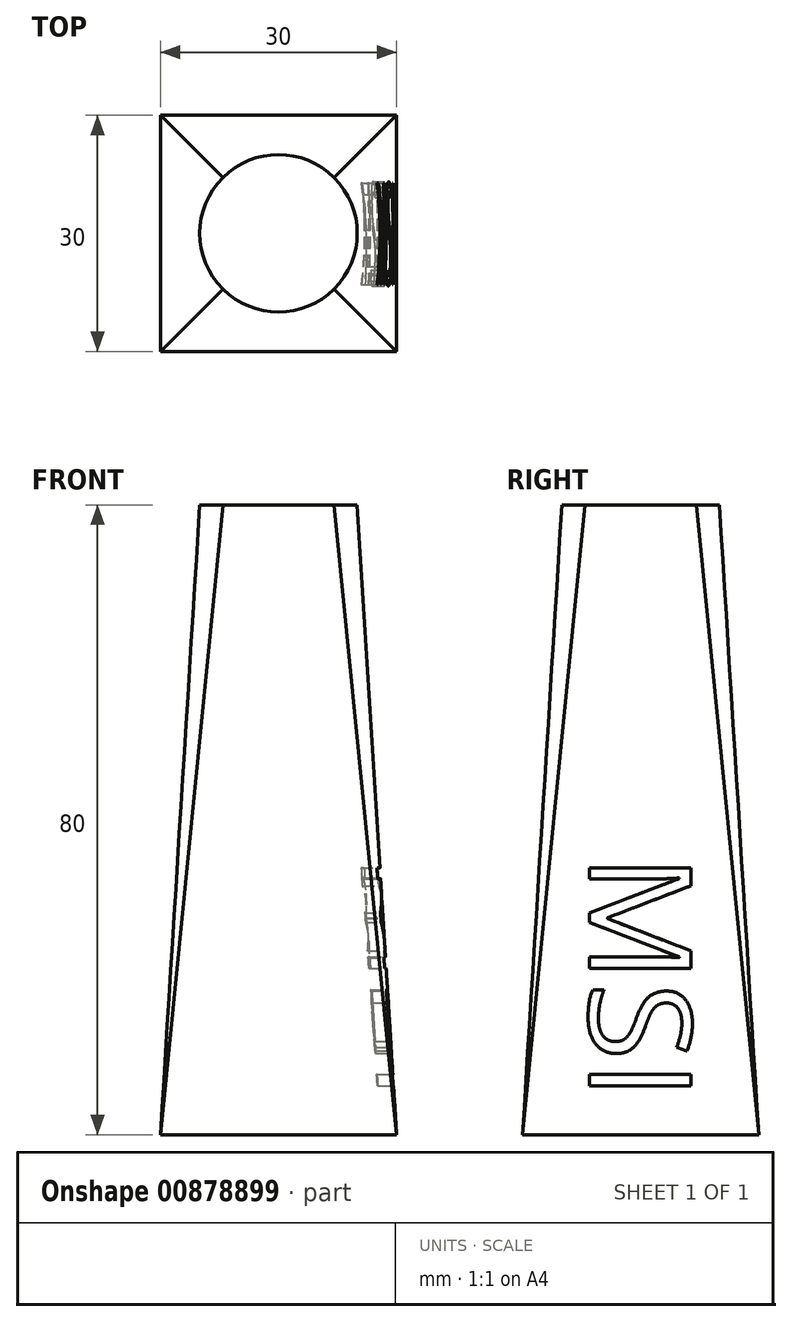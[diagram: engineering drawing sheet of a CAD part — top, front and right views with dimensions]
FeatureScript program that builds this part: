
annotation { "Feature Type Name" : "Feature", "Feature Type Description" : "" }
export const myFeature = defineFeature(function(context is Context, id is Id, definition is map)
    precondition{}
    {
        {
            var Q0;
            Q0=qCreatedBy(makeId("Top.planeOp"),FACE);
            var sketch = newSketch(context, id + "F0", { "sketchPlane" : qUnion([Q0])});
            skLineSegment(sketch, "E0.bottom", {"start": v(15, -15) * mm, "end": v(-15, -15) * mm});
            skLineSegment(sketch, "E0.top", {"start": v(15, 15) * mm, "end": v(-15, 15) * mm});
            skLineSegment(sketch, "E0.left", {"start": v(15, -15) * mm, "end": v(15, 15) * mm});
            skLineSegment(sketch, "E0.right", {"start": v(-15, -15) * mm, "end": v(-15, 15) * mm});
            skPoint(sketch, "E0.middle", {"position": v(0, 0) * mm});
            skSolve(sketch);
        }
        {
            var Q0;
            Q0=qCreatedBy(makeId("Top.planeOp"),FACE);
            cPlane(context, id + "F1", {"entities" : qUnion([Q0]), "cplaneType" : CPlaneType.OFFSET, "offset" : 80 * mm, "width" : 150 * mm, "height" : 150 * mm});
        }
        {
            var Q0;
            Q0=qCreatedBy(id+"F1.planeOp",FACE);
            var sketch = newSketch(context, id + "F2", { "sketchPlane" : qUnion([Q0])});
            skCircle(sketch, "E1", {"center": v(0, 0) * mm, "radius": 10 * mm});
            skSolve(sketch);
        }
        {
            var Q0;
            Q0=makeQuery(id+"F0.imprint","IMPRINT",FACE,{"disambiguationData":[TD([[makeQuery(id+"F0.imprint","IMPRINT",EDGE,{"derivedFrom":sQuery(id+"F0.wireOp",EDGE,"E0.bottom")}),-1.0]])]});
            var Q1;
            Q1=makeQuery(id+"F2.imprint","IMPRINT",FACE,{"disambiguationData":[TD([[makeQuery(id+"F2.imprint","IMPRINT",EDGE,{"derivedFrom":sQuery(id+"F2.wireOp",EDGE,"E1")}),1.0]])]});
            loft(context, id + "F3", {"sheetProfilesArray" : [{ "sheetProfileEntities" : qUnion([Q0]) }, { "sheetProfileEntities" : qUnion([Q1]) }]});
        }
        {
            var Q0;
            Q0=qCreatedBy(makeId("Right.planeOp"),FACE);
            cPlane(context, id + "F4", {"entities" : qUnion([Q0]), "cplaneType" : CPlaneType.OFFSET, "offset" : 50 * mm, "width" : 150 * mm, "height" : 150 * mm});
        }
        {
            var Q0;
            Q0=qCreatedBy(id+"F4.planeOp",FACE);
            var sketch = newSketch(context, id + "F5", { "sketchPlane" : qUnion([Q0])});
            skText(sketch, "E2", { "text": "MSI", "fontName": "OpenSans-Regular.ttf"});
            const initialGuessF5  = {"E2": [-0.0065, 0.03565, 0, -1, 0.013]};
            skSetInitialGuess(sketch, initialGuessF5);
            skSolve(sketch);
        }
        {
            var Q0;
            Q0 = qSketchRegion(id + "F5", true);
            var Q1;
            Q1 = qConstructionFilter(qBodyType(qCreatedBy(id + "F5" ,EDGE), BodyType.WIRE), ConstructionObject.NO);
            var Q2;
            Q2=makeQuery(id+"F3.opLoft","SWEPT_FACE",FACE,{"disambiguationData":[OSD([sQuery(id+"F0.wireOp",EDGE,"E0.bottom"),sQuery(id+"F0.wireOp",EDGE,"E0.top"),sQuery(id+"F0.wireOp",EDGE,"E0.left"),sQuery(id+"F2.wireOp",EDGE,"E1")])]});
            var Q3;
            Q3=makeQuery(id+"F3.opLoft","SWEPT_BODY",BODY,{"disambiguationData":[OSD([makeQuery(id+"F0.imprint","IMPRINT",FACE,{"disambiguationData":[TD([[makeQuery(id+"F0.imprint","IMPRINT",EDGE,{"derivedFrom":sQuery(id+"F0.wireOp",EDGE,"E0.bottom")}),-1.0]])]}),makeQuery(id+"F2.imprint","IMPRINT",FACE,{"disambiguationData":[TD([[makeQuery(id+"F2.imprint","IMPRINT",EDGE,{"derivedFrom":sQuery(id+"F2.wireOp",EDGE,"E1")}),1.0]])]})])]});
            extrude(context, id + "F6", {"entities" : qUnion([Q0]), "operationType" : NewBodyOperationType.REMOVE, "surfaceEntities" : qUnion([Q1]), "endBound" : BoundingType.UP_TO_BODY, "oppositeDirection" : true, "depth" : 25 * mm, "endBoundEntityFace" : qUnion([Q2]), "endBoundEntityBody" : qUnion([Q3]), "hasOffset" : true, "offsetDistance" : 2 * mm, "offsetOppositeDirection" : true});
        }
    });
